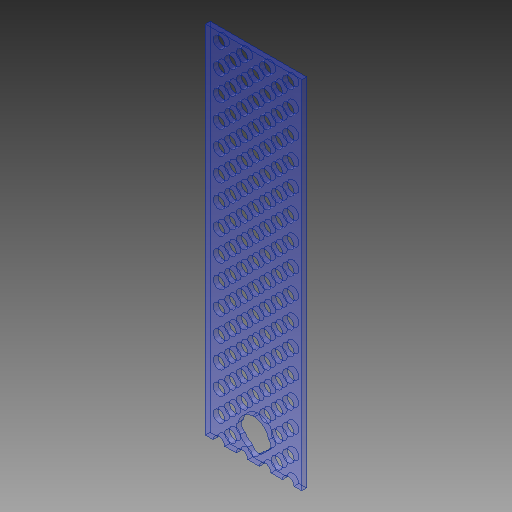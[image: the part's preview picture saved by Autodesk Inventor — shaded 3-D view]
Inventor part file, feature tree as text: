
AUTODESK INVENTOR PART (.ipt)
format: ipt  version: 2018.1 (Build 221171000, 171)  size: 326,656 bytes
history: native  units: mm
features: other x4, extrude x3, sketch x3, reference x1
ambient origin geometry x8: Origin, YZ Plane, XZ Plane, XY Plane, X Axis, Y Axis, Z Axis, Center Point
bodies: Solid1 (feature_tree)
feature tree (11):
  parser-record x2  (decoder bookkeeping rows leaked as tree rows — omitted from the tree; the rows remain in map.json)
  extrude  "Extrusion1"  Depth=370.0mm
  sketch  "Sketch2"  dims[d2=5.0mm d3=0.0mm]
  extrude  "Extrusion3"  TaperAngle=0.0deg  [1 undecoded]
  extrude  "Extrusion4"  TaperAngle=0.0deg  [1 undecoded]
  sketch  "Sketch1"  dims[d0=100.0mm d1=370.0mm]
  sketch  "Sketch3"  dims[d24=13.9375mm d25=0.0mm d26=12.020815mm d27=12.020815mm d30=5.0mm d31=0.0mm d32=160.0mm d34=24.041631mm d35=40.0mm d37=24.041631mm d40=150.0mm d42=24.041631mm d43=30.0mm d45=24.041631mm d48=13.937608mm d49=5.0mm d50=0.0mm]
  reference  "Reference1"
  other  "tank_assembly.iam"
  other  "tank_back:1"
note: 2 required parameter values undecoded (feature->parameter linkage not recoverable at this tier; creation-order binding heuristic only, values carry confidence <= 0.55)
note: 2 file-system paths scrubbed to <path> (originals preserved in map.json)
